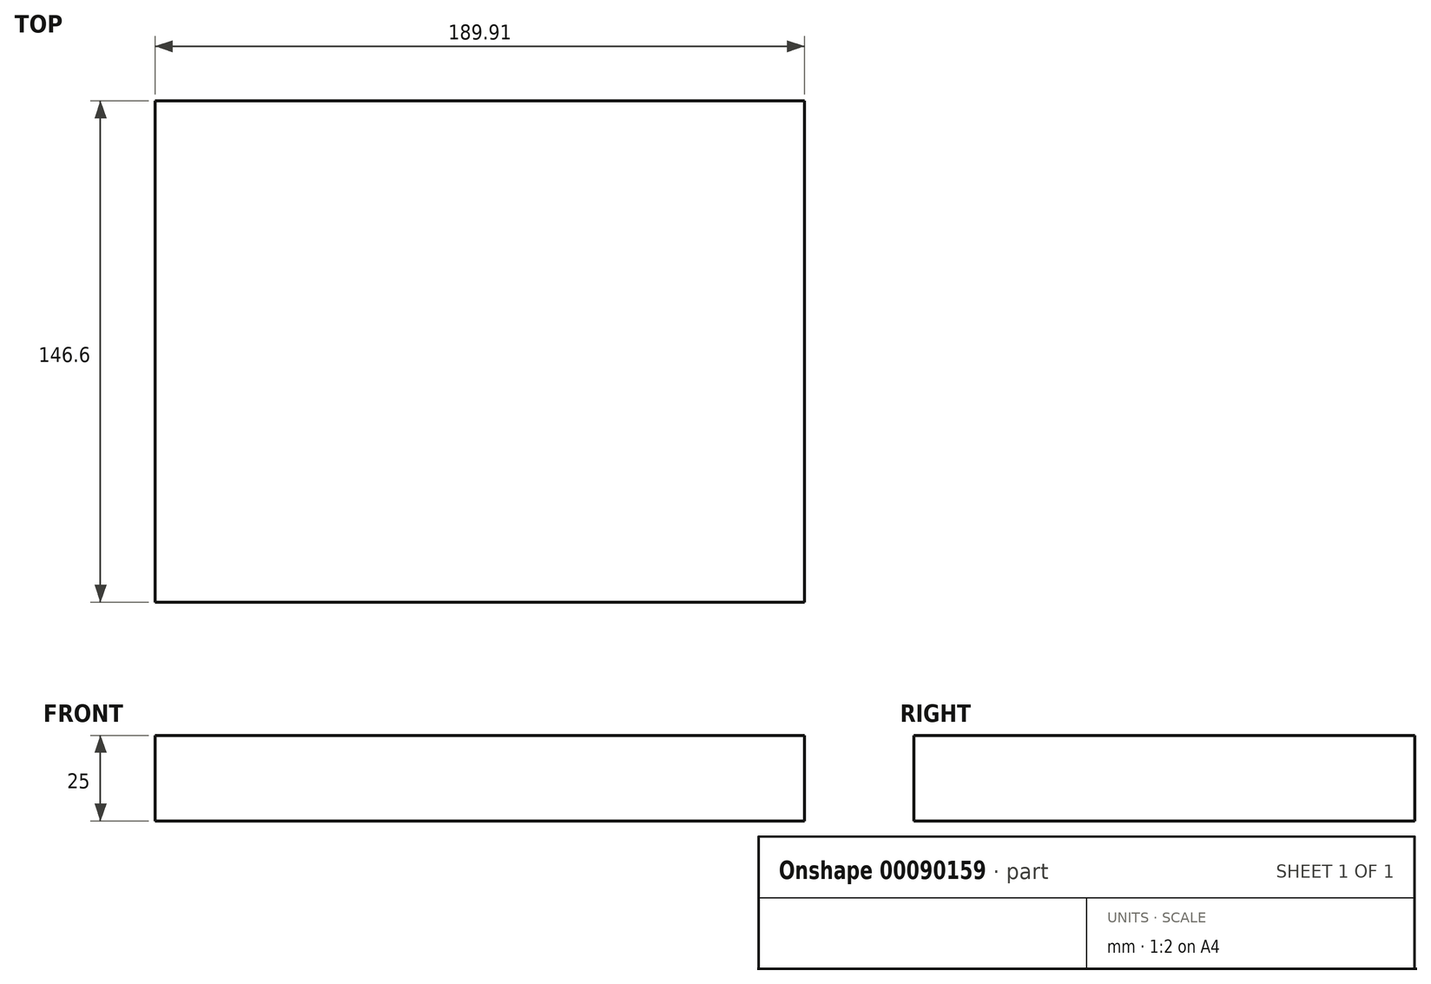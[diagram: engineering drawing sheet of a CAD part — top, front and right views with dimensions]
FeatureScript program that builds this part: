
annotation { "Feature Type Name" : "Feature", "Feature Type Description" : "" }
export const myFeature = defineFeature(function(context is Context, id is Id, definition is map)
    precondition{}
    {
        {
            var Q0;
            Q0=qCreatedBy(makeId("Top.planeOp"),FACE);
            var sketch = newSketch(context, id + "F0", { "sketchPlane" : qUnion([Q0])});
            skLineSegment(sketch, "E0.bottom", {"start": v(-99.9, 79.32) * mm, "end": v(90, 79.32) * mm});
            skLineSegment(sketch, "E0.top", {"start": v(-99.9, -67.28) * mm, "end": v(90, -67.28) * mm});
            skLineSegment(sketch, "E0.left", {"start": v(-99.9, 79.32) * mm, "end": v(-99.9, -67.28) * mm});
            skLineSegment(sketch, "E0.right", {"start": v(90, 79.32) * mm, "end": v(90, -67.28) * mm});
            skSolve(sketch);
        }
        {
            var Q0;
            Q0 = qSketchRegion(id + "F0", true);
            extrude(context, id + "F1", {"entities" : qUnion([Q0]), "depth" : 25 * mm});
        }
    });
